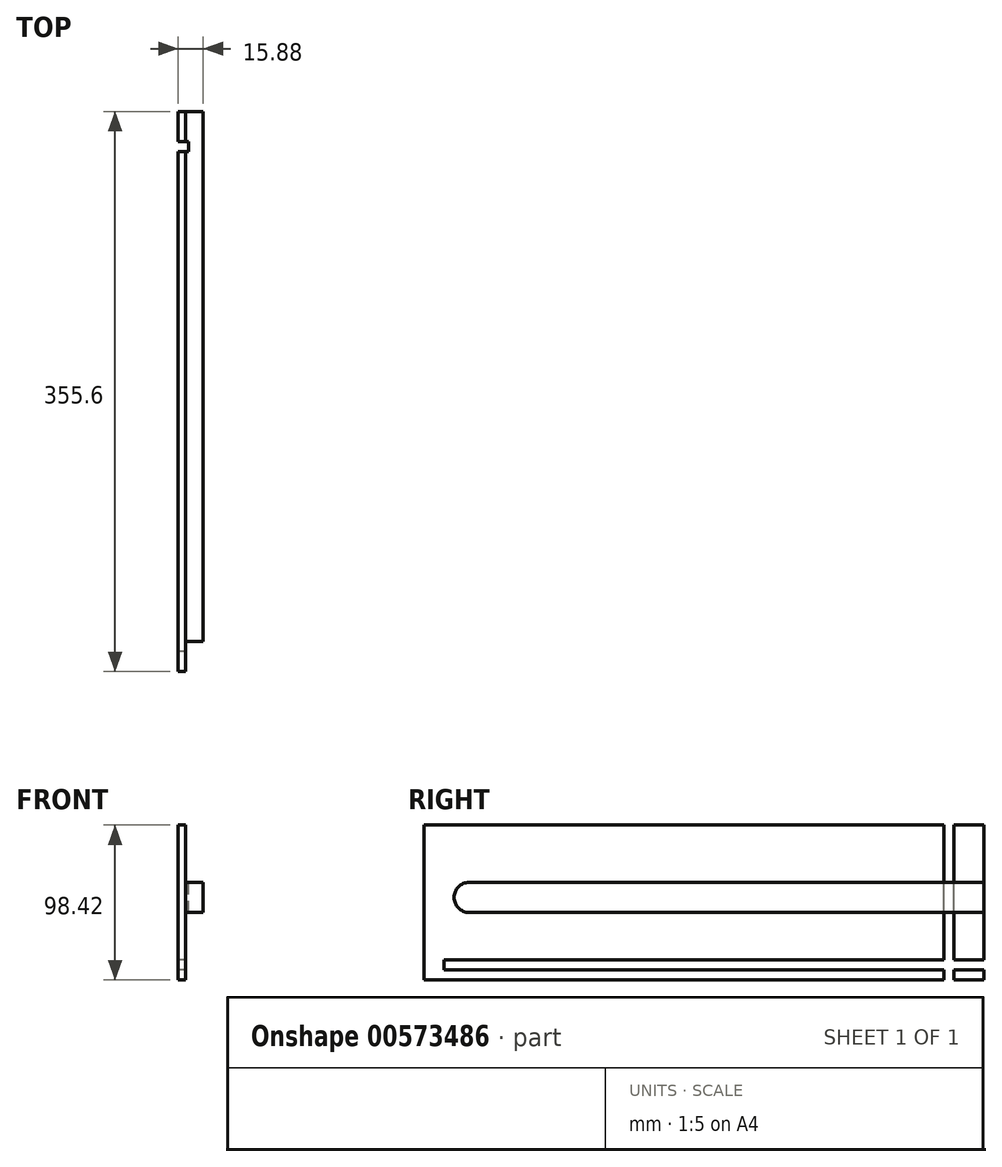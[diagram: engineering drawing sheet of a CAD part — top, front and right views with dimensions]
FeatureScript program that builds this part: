
annotation { "Feature Type Name" : "Feature", "Feature Type Description" : "" }
export const myFeature = defineFeature(function(context is Context, id is Id, definition is map)
    precondition{}
    {
        {
            var Q0;
            Q0=qCreatedBy(makeId("Right.planeOp"),FACE);
            var sketch = newSketch(context, id + "F0", { "sketchPlane" : qUnion([Q0])});
            skLineSegment(sketch, "E0.bottom", {"start": v(0, 0) * mm, "end": v(355.6, 0) * mm});
            skLineSegment(sketch, "E0.top", {"start": v(0, 98.43) * mm, "end": v(355.6, 98.43) * mm});
            skLineSegment(sketch, "E0.left", {"start": v(0, 0) * mm, "end": v(0, 98.43) * mm});
            skLineSegment(sketch, "E0.right", {"start": v(355.6, 0) * mm, "end": v(355.6, 98.43) * mm});
            skSolve(sketch);
        }
        {
            var Q0;
            Q0=makeQuery(id+"F0.imprint","IMPRINT",FACE,{"disambiguationData":[TD([[makeQuery(id+"F0.imprint","IMPRINT",EDGE,{"derivedFrom":sQuery(id+"F0.wireOp",EDGE,"E0.bottom")}),1.0]])]});
            extrude(context, id + "F1", {"entities" : qUnion([Q0]), "depth" : 15.88 * mm, "offsetDistance" : 25.4 * mm});
        }
        {
            var Q0;
            Q0=makeQuery(id+"F1.opExtrude","CAP_FACE",FACE,{"disambiguationData":[OSD([sQuery(id+"F0.wireOp",EDGE,"E0.bottom"),sQuery(id+"F0.wireOp",EDGE,"E0.top"),sQuery(id+"F0.wireOp",EDGE,"E0.left"),sQuery(id+"F0.wireOp",EDGE,"E0.right")])],"isStart":false});
            var sketch = newSketch(context, id + "F2", { "sketchPlane" : qUnion([Q0])});
            skLineSegment(sketch, "E1", {"start": v(28.58, 52.39) * mm, "end": v(355.6, 52.39) * mm});
            skArc(sketch, "E2.0.startCap", {"start": v(28.57, 42.86) * mm, "mid": v(19.05, 52.39) * mm, "end": v(28.57, 61.91) * mm});
            skArc(sketch, "E2.0.endCap", {"start": v(355.6, 61.91) * mm, "mid": v(365.13, 52.39) * mm, "end": v(355.6, 42.86) * mm});
            skLineSegment(sketch, "E2.0.left", {"start": v(28.58, 61.91) * mm, "end": v(355.6, 61.91) * mm});
            skLineSegment(sketch, "E2.0.right", {"start": v(28.58, 42.86) * mm, "end": v(355.6, 42.86) * mm});
            skSolve(sketch);
        }
        {
            var Q0;
            Q0=makeQuery(id+"F2.imprint","IMPRINT",FACE,{"disambiguationData":[TD([[makeQuery(id+"F2.imprint","IMPRINT",EDGE,{"derivedFrom":sQuery(id+"F2.wireOp",EDGE,"E2.0.startCap")}),-1.0]])]});
            extrude(context, id + "F3", {"entities" : qUnion([Q0]), "operationType" : NewBodyOperationType.REMOVE, "oppositeDirection" : true, "depth" : 11.1 * mm, "offsetDistance" : 25.4 * mm});
        }
        {
            var Q0;
            Q0=makeQuery(id+"F1.opExtrude","CAP_FACE",FACE,{"disambiguationData":[OSD([sQuery(id+"F0.wireOp",EDGE,"E0.bottom"),sQuery(id+"F0.wireOp",EDGE,"E0.top"),sQuery(id+"F0.wireOp",EDGE,"E0.left"),sQuery(id+"F0.wireOp",EDGE,"E0.right")])],"isStart":true});
            var sketch = newSketch(context, id + "F4", { "sketchPlane" : qUnion([Q0])});
            skLineSegment(sketch, "E3.bottom", {"start": v(-355.6, 6.35) * mm, "end": v(-12.7, 6.35) * mm});
            skLineSegment(sketch, "E3.top", {"start": v(-355.6, 12.7) * mm, "end": v(-12.7, 12.7) * mm});
            skLineSegment(sketch, "E3.left", {"start": v(-355.6, 6.35) * mm, "end": v(-355.6, 12.7) * mm});
            skLineSegment(sketch, "E3.right", {"start": v(-12.7, 6.35) * mm, "end": v(-12.7, 12.7) * mm});
            skSolve(sketch);
        }
        {
            var Q0;
            Q0=makeQuery(id+"F4.imprint","IMPRINT",FACE,{"disambiguationData":[TD([[makeQuery(id+"F4.imprint","IMPRINT",EDGE,{"derivedFrom":sQuery(id+"F4.wireOp",EDGE,"E3.bottom")}),1.0]])]});
            extrude(context, id + "F5", {"entities" : qUnion([Q0]), "operationType" : NewBodyOperationType.REMOVE, "oppositeDirection" : true, "depth" : 6.35 * mm, "offsetDistance" : 25.4 * mm});
        }
        {
            var Q0;
            Q0=makeQuery(id+"F1.opExtrude","SWEPT_FACE",FACE,{"disambiguationData":[OSD([sQuery(id+"F0.wireOp",EDGE,"E0.top")])]});
            var sketch = newSketch(context, id + "F6", { "sketchPlane" : qUnion([Q0])});
            skLineSegment(sketch, "E4.bottom", {"start": v(0, 336.55) * mm, "end": v(6.6, 336.55) * mm});
            skLineSegment(sketch, "E4.top", {"start": v(0, 330.2) * mm, "end": v(6.6, 330.2) * mm});
            skLineSegment(sketch, "E4.left", {"start": v(0, 336.55) * mm, "end": v(0, 330.2) * mm});
            skLineSegment(sketch, "E4.right", {"start": v(6.6, 336.55) * mm, "end": v(6.6, 330.2) * mm});
            skSolve(sketch);
        }
        {
            var Q0;
            Q0=makeQuery(id+"F6.imprint","IMPRINT",FACE,{"disambiguationData":[TD([[makeQuery(id+"F6.imprint","IMPRINT",EDGE,{"derivedFrom":sQuery(id+"F6.wireOp",EDGE,"E4.bottom")}),-1.0]])]});
            var Q1;
            Q1=makeQuery(id+"F1.opExtrude","SWEPT_FACE",FACE,{"disambiguationData":[OSD([sQuery(id+"F0.wireOp",EDGE,"E0.bottom")])]});
            extrude(context, id + "F7", {"entities" : qUnion([Q0]), "operationType" : NewBodyOperationType.REMOVE, "endBound" : BoundingType.UP_TO_SURFACE, "oppositeDirection" : true, "depth" : 25.4 * mm, "endBoundEntityFace" : qUnion([Q1]), "offsetDistance" : 25.4 * mm});
        }
    });
